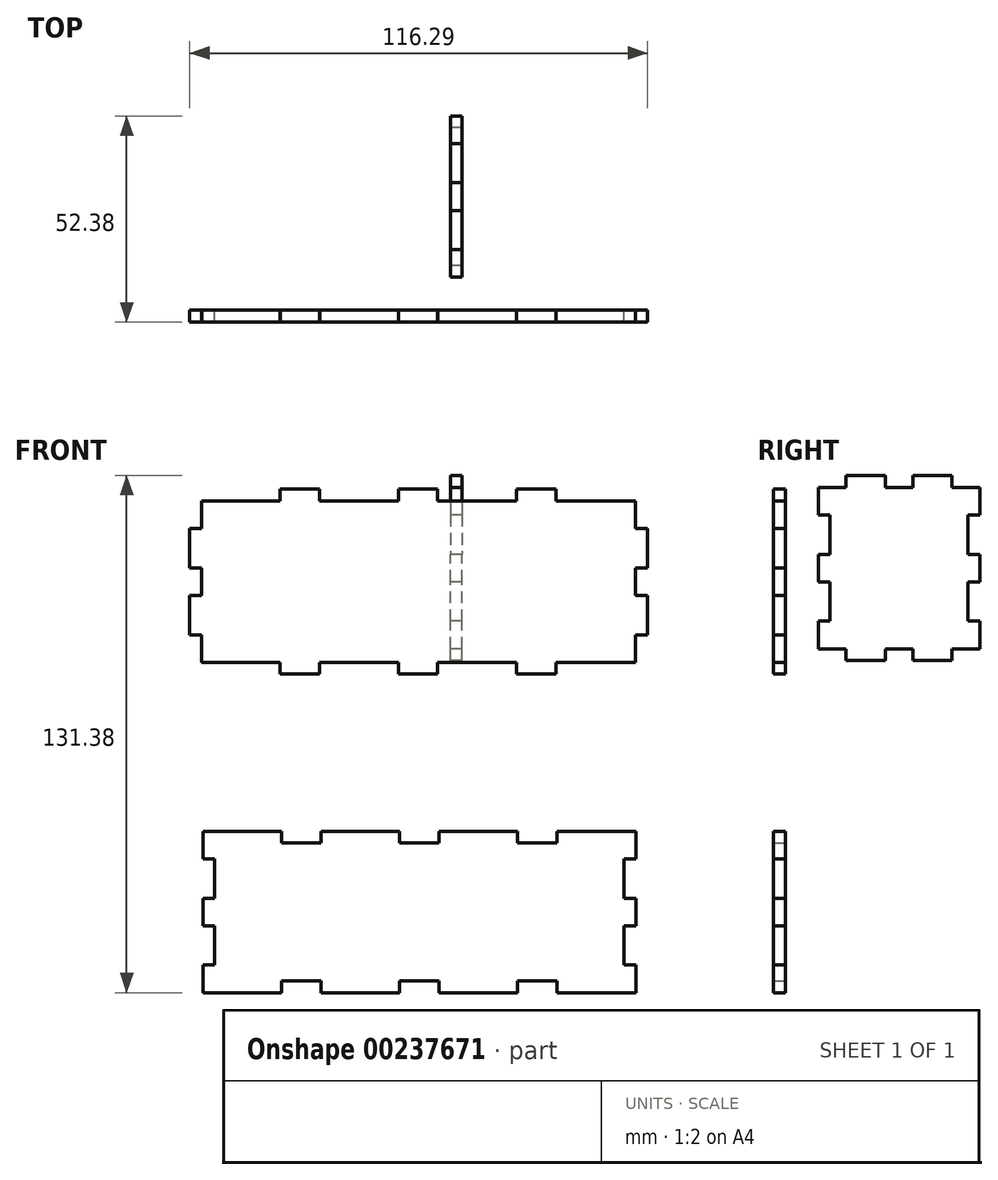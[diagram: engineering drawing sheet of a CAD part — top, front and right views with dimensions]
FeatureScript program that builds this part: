
annotation { "Feature Type Name" : "Feature", "Feature Type Description" : "" }
export const myFeature = defineFeature(function(context is Context, id is Id, definition is map)
    precondition{}
    {
        {
            var Q0;
            Q0=qCreatedBy(makeId("Front.planeOp"),FACE);
            var sketch = newSketch(context, id + "F0", { "sketchPlane" : qUnion([Q0])});
            skLineSegment(sketch, "E0", {"start": v(-62.87, -67.73) * mm, "end": v(-62.87, -60.73) * mm});
            skLineSegment(sketch, "E1", {"start": v(-62.87, -60.73) * mm, "end": v(-59.87, -60.73) * mm});
            skLineSegment(sketch, "E2", {"start": v(-59.87, -60.73) * mm, "end": v(-59.87, -50.73) * mm});
            skLineSegment(sketch, "E3", {"start": v(-59.87, -50.73) * mm, "end": v(-62.87, -50.73) * mm});
            skLineSegment(sketch, "E4", {"start": v(-62.87, -50.73) * mm, "end": v(-62.87, -43.73) * mm});
            skLineSegment(sketch, "E5", {"start": v(-62.87, -43.73) * mm, "end": v(-59.87, -43.73) * mm});
            skLineSegment(sketch, "E6", {"start": v(-59.87, -43.73) * mm, "end": v(-59.87, -33.73) * mm});
            skLineSegment(sketch, "E7", {"start": v(-59.87, -33.73) * mm, "end": v(-62.87, -33.73) * mm});
            skLineSegment(sketch, "E8", {"start": v(-62.87, -33.73) * mm, "end": v(-62.87, -26.73) * mm});
            skLineSegment(sketch, "E9", {"start": v(-62.87, -26.73) * mm, "end": v(-42.87, -26.73) * mm});
            skLineSegment(sketch, "E10", {"start": v(-42.87, -26.73) * mm, "end": v(-42.87, -29.73) * mm});
            skLineSegment(sketch, "E11", {"start": v(-42.87, -29.73) * mm, "end": v(-32.87, -29.73) * mm});
            skLineSegment(sketch, "E12", {"start": v(-32.87, -29.73) * mm, "end": v(-32.87, -26.73) * mm});
            skLineSegment(sketch, "E13", {"start": v(-32.87, -26.73) * mm, "end": v(-12.87, -26.73) * mm});
            skLineSegment(sketch, "E14", {"start": v(-12.87, -26.73) * mm, "end": v(-12.87, -29.73) * mm});
            skLineSegment(sketch, "E15", {"start": v(-12.87, -29.73) * mm, "end": v(-2.87, -29.73) * mm});
            skLineSegment(sketch, "E16", {"start": v(-2.87, -29.73) * mm, "end": v(-2.87, -26.73) * mm});
            skLineSegment(sketch, "E17", {"start": v(-2.87, -26.73) * mm, "end": v(17.13, -26.73) * mm});
            skLineSegment(sketch, "E18", {"start": v(17.13, -26.73) * mm, "end": v(17.13, -29.73) * mm});
            skLineSegment(sketch, "E19", {"start": v(17.13, -29.73) * mm, "end": v(27.13, -29.73) * mm});
            skLineSegment(sketch, "E20", {"start": v(27.13, -29.73) * mm, "end": v(27.13, -26.73) * mm});
            skLineSegment(sketch, "E21", {"start": v(27.13, -26.73) * mm, "end": v(47.13, -26.73) * mm});
            skLineSegment(sketch, "E22", {"start": v(47.13, -26.73) * mm, "end": v(47.13, -33.73) * mm});
            skLineSegment(sketch, "E23", {"start": v(47.13, -33.73) * mm, "end": v(44.13, -33.73) * mm});
            skLineSegment(sketch, "E24", {"start": v(44.13, -33.73) * mm, "end": v(44.13, -43.73) * mm});
            skLineSegment(sketch, "E25", {"start": v(44.13, -43.73) * mm, "end": v(47.13, -43.73) * mm});
            skLineSegment(sketch, "E26", {"start": v(47.13, -43.73) * mm, "end": v(47.13, -51.3) * mm});
            skLineSegment(sketch, "E27.MirrorCS", {"start": v(-59.87, -43.73) * mm, "end": v(-62.87, -43.73) * mm});
            skLineSegment(sketch, "E28.MirrorCS", {"start": v(-62.87, -50.73) * mm, "end": v(-59.87, -50.73) * mm});
            skLineSegment(sketch, "E29.MirrorCS", {"start": v(17.13, -67.73) * mm, "end": v(17.13, -64.73) * mm});
            skLineSegment(sketch, "E30.MirrorCS", {"start": v(-42.87, -67.73) * mm, "end": v(-42.87, -64.73) * mm});
            skLineSegment(sketch, "E31.MirrorCS", {"start": v(-59.87, -60.73) * mm, "end": v(-62.87, -60.73) * mm});
            skLineSegment(sketch, "E32.MirrorCS", {"start": v(44.13, -50.73) * mm, "end": v(47.13, -50.73) * mm});
            skLineSegment(sketch, "E33.MirrorCS", {"start": v(-12.87, -67.73) * mm, "end": v(-12.87, -64.73) * mm});
            skLineSegment(sketch, "E34.MirrorCS", {"start": v(47.13, -60.73) * mm, "end": v(44.13, -60.73) * mm});
            skLineSegment(sketch, "E35.MirrorCS", {"start": v(27.13, -64.73) * mm, "end": v(27.13, -67.73) * mm});
            skLineSegment(sketch, "E36.MirrorCS", {"start": v(-32.87, -64.73) * mm, "end": v(-32.87, -67.73) * mm});
            skLineSegment(sketch, "E37.MirrorCS", {"start": v(-2.87, -64.73) * mm, "end": v(-2.87, -67.73) * mm});
            skLineSegment(sketch, "E38.MirrorCS", {"start": v(-12.87, -64.73) * mm, "end": v(-2.87, -64.73) * mm});
            skLineSegment(sketch, "E39.MirrorCS", {"start": v(-42.87, -64.73) * mm, "end": v(-32.87, -64.73) * mm});
            skLineSegment(sketch, "E40.MirrorCS", {"start": v(17.13, -64.73) * mm, "end": v(27.13, -64.73) * mm});
            skLineSegment(sketch, "E41.MirrorCS", {"start": v(-62.87, -43.73) * mm, "end": v(-62.87, -50.73) * mm});
            skLineSegment(sketch, "E42.MirrorCS", {"start": v(44.13, -60.73) * mm, "end": v(44.13, -50.73) * mm});
            skLineSegment(sketch, "E43.MirrorCS", {"start": v(27.13, -67.73) * mm, "end": v(47.13, -67.73) * mm});
            skLineSegment(sketch, "E44.MirrorCS", {"start": v(-32.87, -67.73) * mm, "end": v(-12.87, -67.73) * mm});
            skLineSegment(sketch, "E45.MirrorCS", {"start": v(-2.87, -67.73) * mm, "end": v(17.13, -67.73) * mm});
            skLineSegment(sketch, "E46.MirrorCS", {"start": v(-62.87, -60.73) * mm, "end": v(-62.87, -67.73) * mm});
            skLineSegment(sketch, "E47.MirrorCS", {"start": v(-62.87, -67.73) * mm, "end": v(-42.87, -67.73) * mm});
            skLineSegment(sketch, "E48.MirrorCS", {"start": v(47.13, -50.73) * mm, "end": v(47.13, -43.16) * mm});
            skLineSegment(sketch, "E49.MirrorCS", {"start": v(47.13, -67.73) * mm, "end": v(47.13, -60.73) * mm});
            skLineSegment(sketch, "E50.MirrorCS", {"start": v(-59.87, -50.73) * mm, "end": v(-59.87, -60.73) * mm});
            skLineSegment(sketch, "E51", {"start": v(-63.18, 57.19) * mm, "end": v(-43.18, 57.19) * mm});
            skLineSegment(sketch, "E52", {"start": v(-43.18, 57.19) * mm, "end": v(-43.18, 60.19) * mm});
            skLineSegment(sketch, "E53", {"start": v(-43.18, 60.19) * mm, "end": v(-33.18, 60.19) * mm});
            skLineSegment(sketch, "E54", {"start": v(-33.18, 60.19) * mm, "end": v(-33.18, 57.19) * mm});
            skLineSegment(sketch, "E55", {"start": v(-33.18, 57.19) * mm, "end": v(-13.18, 57.19) * mm});
            skLineSegment(sketch, "E56", {"start": v(-13.18, 57.19) * mm, "end": v(-13.18, 60.19) * mm});
            skLineSegment(sketch, "E57", {"start": v(-13.18, 60.19) * mm, "end": v(-3.18, 60.19) * mm});
            skLineSegment(sketch, "E58", {"start": v(-3.18, 60.19) * mm, "end": v(-3.18, 57.19) * mm});
            skLineSegment(sketch, "E59", {"start": v(-3.18, 57.19) * mm, "end": v(16.82, 57.19) * mm});
            skLineSegment(sketch, "E60", {"start": v(16.82, 57.19) * mm, "end": v(16.82, 60.19) * mm});
            skLineSegment(sketch, "E61", {"start": v(16.82, 60.19) * mm, "end": v(26.82, 60.19) * mm});
            skLineSegment(sketch, "E62", {"start": v(26.82, 60.19) * mm, "end": v(26.82, 57.19) * mm});
            skLineSegment(sketch, "E63", {"start": v(26.82, 57.19) * mm, "end": v(47.1, 57.19) * mm});
            skLineSegment(sketch, "E64", {"start": v(47.1, 57.19) * mm, "end": v(47.1, 50.19) * mm});
            skLineSegment(sketch, "E65", {"start": v(47.1, 50.19) * mm, "end": v(50.1, 50.19) * mm});
            skLineSegment(sketch, "E66", {"start": v(50.1, 50.19) * mm, "end": v(50.1, 40.19) * mm});
            skLineSegment(sketch, "E67", {"start": v(50.1, 40.19) * mm, "end": v(47.1, 40.19) * mm});
            skLineSegment(sketch, "E68", {"start": v(47.1, 40.19) * mm, "end": v(47.1, 33.19) * mm});
            skLineSegment(sketch, "E69", {"start": v(47.1, 33.19) * mm, "end": v(50.1, 33.19) * mm});
            skLineSegment(sketch, "E70", {"start": v(-63.18, 57.19) * mm, "end": v(-63.18, 50.19) * mm});
            skLineSegment(sketch, "E71", {"start": v(-63.18, 50.19) * mm, "end": v(-66.18, 50.19) * mm});
            skLineSegment(sketch, "E72", {"start": v(-66.18, 50.19) * mm, "end": v(-66.18, 40.19) * mm});
            skLineSegment(sketch, "E73", {"start": v(-66.18, 40.19) * mm, "end": v(-63.18, 40.19) * mm});
            skLineSegment(sketch, "E74", {"start": v(-63.18, 40.19) * mm, "end": v(-63.18, 33.19) * mm});
            skPoint(sketch, "E75.endSnap0", {"position": v(47.1, 36.69) * mm});
            skLineSegment(sketch, "E76.MirrorCS", {"start": v(47.1, 23.19) * mm, "end": v(50.1, 23.19) * mm});
            skLineSegment(sketch, "E77.MirrorCS", {"start": v(-43.18, 13.19) * mm, "end": v(-33.18, 13.19) * mm});
            skLineSegment(sketch, "E78.MirrorCS", {"start": v(26.82, 13.19) * mm, "end": v(26.82, 16.19) * mm});
            skLineSegment(sketch, "E79.MirrorCS", {"start": v(-66.18, 23.19) * mm, "end": v(-66.18, 33.19) * mm});
            skLineSegment(sketch, "E80.MirrorCS", {"start": v(-13.18, 16.19) * mm, "end": v(-13.18, 13.19) * mm});
            skLineSegment(sketch, "E81.MirrorCS", {"start": v(47.1, 16.19) * mm, "end": v(47.1, 23.19) * mm});
            skLineSegment(sketch, "E82.MirrorCS", {"start": v(-43.18, 16.19) * mm, "end": v(-43.18, 13.19) * mm});
            skLineSegment(sketch, "E83.MirrorCS", {"start": v(16.82, 13.19) * mm, "end": v(26.82, 13.19) * mm});
            skLineSegment(sketch, "E84.MirrorCS", {"start": v(-63.18, 23.19) * mm, "end": v(-66.18, 23.19) * mm});
            skLineSegment(sketch, "E85.MirrorCS", {"start": v(-33.18, 16.19) * mm, "end": v(-13.18, 16.19) * mm});
            skLineSegment(sketch, "E86.MirrorCS", {"start": v(-3.18, 16.19) * mm, "end": v(16.82, 16.19) * mm});
            skLineSegment(sketch, "E87.MirrorCS", {"start": v(26.82, 16.19) * mm, "end": v(47.1, 16.19) * mm});
            skLineSegment(sketch, "E88.MirrorCS", {"start": v(-63.18, 16.19) * mm, "end": v(-43.18, 16.19) * mm});
            skLineSegment(sketch, "E89.MirrorCS", {"start": v(50.1, 33.19) * mm, "end": v(47.1, 33.19) * mm});
            skLineSegment(sketch, "E90.MirrorCS", {"start": v(16.82, 16.19) * mm, "end": v(16.82, 13.19) * mm});
            skLineSegment(sketch, "E91.MirrorCS", {"start": v(-63.18, 16.19) * mm, "end": v(-63.18, 23.19) * mm});
            skLineSegment(sketch, "E92.MirrorCS", {"start": v(-33.18, 13.19) * mm, "end": v(-33.18, 16.19) * mm});
            skLineSegment(sketch, "E93.MirrorCS", {"start": v(-3.18, 13.19) * mm, "end": v(-3.18, 16.19) * mm});
            skLineSegment(sketch, "E94.MirrorCS", {"start": v(50.1, 23.19) * mm, "end": v(50.1, 33.19) * mm});
            skLineSegment(sketch, "E95.MirrorCS", {"start": v(-66.18, 33.19) * mm, "end": v(-63.18, 33.19) * mm});
            skLineSegment(sketch, "E96.MirrorCS", {"start": v(-13.18, 13.19) * mm, "end": v(-3.18, 13.19) * mm});
            skLineSegment(sketch, "E97.MirrorCS", {"start": v(-62.87, 117.1) * mm, "end": v(-62.87, 124.1) * mm, "construction": true});
            skLineSegment(sketch, "E98.MirrorCS", {"start": v(47.13, 117.1) * mm, "end": v(47.13, 124.67) * mm, "construction": true});
            skLineSegment(sketch, "E99.MirrorCS", {"start": v(-59.87, 124.1) * mm, "end": v(-59.87, 134.1) * mm, "construction": true});
            skLineSegment(sketch, "E100.MirrorCS", {"start": v(-62.87, 134.1) * mm, "end": v(-62.87, 141.1) * mm, "construction": true});
            skLineSegment(sketch, "E101.MirrorCS", {"start": v(-62.87, 134.1) * mm, "end": v(-59.87, 134.1) * mm, "construction": true});
            skLineSegment(sketch, "E102.MirrorCS", {"start": v(-62.87, 124.1) * mm, "end": v(-59.87, 124.1) * mm, "construction": true});
            skLineSegment(sketch, "E103.MirrorCS", {"start": v(-59.87, 117.1) * mm, "end": v(-62.87, 117.1) * mm, "construction": true});
            skLineSegment(sketch, "E104.MirrorCS", {"start": v(-12.87, 141.1) * mm, "end": v(-12.87, 138.1) * mm, "construction": true});
            skLineSegment(sketch, "E105.MirrorCS", {"start": v(47.13, 141.1) * mm, "end": v(47.13, 134.1) * mm, "construction": true});
            skLineSegment(sketch, "E106.MirrorCS", {"start": v(17.13, 100.1) * mm, "end": v(17.13, 103.1) * mm, "construction": true});
            skLineSegment(sketch, "E107.MirrorCS", {"start": v(44.13, 117.1) * mm, "end": v(47.13, 117.1) * mm, "construction": true});
            skLineSegment(sketch, "E108.MirrorCS", {"start": v(17.13, 138.1) * mm, "end": v(27.13, 138.1) * mm, "construction": true});
            skLineSegment(sketch, "E109.MirrorCS", {"start": v(44.13, 124.1) * mm, "end": v(47.13, 124.1) * mm, "construction": true});
            skLineSegment(sketch, "E110.MirrorCS", {"start": v(47.13, 124.1) * mm, "end": v(47.13, 116.53) * mm, "construction": true});
            skLineSegment(sketch, "E111.MirrorCS", {"start": v(-2.87, 100.1) * mm, "end": v(17.13, 100.1) * mm, "construction": true});
            skLineSegment(sketch, "E112.MirrorCS", {"start": v(44.13, 107.1) * mm, "end": v(44.13, 117.1) * mm, "construction": true});
            skLineSegment(sketch, "E113.MirrorCS", {"start": v(-42.87, 138.1) * mm, "end": v(-32.87, 138.1) * mm, "construction": true});
            skLineSegment(sketch, "E114.MirrorCS", {"start": v(27.13, 100.1) * mm, "end": v(47.13, 100.1) * mm, "construction": true});
            skLineSegment(sketch, "E115.MirrorCS", {"start": v(17.13, 103.1) * mm, "end": v(27.13, 103.1) * mm, "construction": true});
            skLineSegment(sketch, "E116.MirrorCS", {"start": v(-2.87, 141.1) * mm, "end": v(17.13, 141.1) * mm, "construction": true});
            skLineSegment(sketch, "E117.MirrorCS", {"start": v(-32.87, 138.1) * mm, "end": v(-32.87, 141.1) * mm, "construction": true});
            skLineSegment(sketch, "E118.MirrorCS", {"start": v(17.13, 141.1) * mm, "end": v(17.13, 138.1) * mm, "construction": true});
            skLineSegment(sketch, "E119.MirrorCS", {"start": v(47.13, 134.1) * mm, "end": v(44.13, 134.1) * mm, "construction": true});
            skLineSegment(sketch, "E120.MirrorCS", {"start": v(47.13, 100.1) * mm, "end": v(47.13, 107.1) * mm, "construction": true});
            skLineSegment(sketch, "E121.MirrorCS", {"start": v(-2.87, 138.1) * mm, "end": v(-2.87, 141.1) * mm, "construction": true});
            skLineSegment(sketch, "E122.MirrorCS", {"start": v(-42.87, 141.1) * mm, "end": v(-42.87, 138.1) * mm, "construction": true});
            skLineSegment(sketch, "E123.MirrorCS", {"start": v(-32.87, 100.1) * mm, "end": v(-12.87, 100.1) * mm, "construction": true});
            skLineSegment(sketch, "E124.MirrorCS", {"start": v(-12.87, 100.1) * mm, "end": v(-12.87, 103.1) * mm, "construction": true});
            skLineSegment(sketch, "E125.MirrorCS", {"start": v(-12.87, 103.1) * mm, "end": v(-2.87, 103.1) * mm, "construction": true});
            skLineSegment(sketch, "E126.MirrorCS", {"start": v(44.13, 134.1) * mm, "end": v(44.13, 124.1) * mm, "construction": true});
            skLineSegment(sketch, "E127.MirrorCS", {"start": v(-62.87, 120.6) * mm, "end": v(59.39, 120.6) * mm, "construction": true});
            skLineSegment(sketch, "E128.MirrorCS", {"start": v(-62.87, 141.1) * mm, "end": v(-62.87, 134.1) * mm, "construction": true});
            skLineSegment(sketch, "E129.MirrorCS", {"start": v(-59.87, 134.1) * mm, "end": v(-59.87, 124.1) * mm, "construction": true});
            skLineSegment(sketch, "E130.MirrorCS", {"start": v(-59.87, 124.1) * mm, "end": v(-62.87, 124.1) * mm, "construction": true});
            skLineSegment(sketch, "E131.MirrorCS", {"start": v(-62.87, 117.1) * mm, "end": v(-59.87, 117.1) * mm, "construction": true});
            skLineSegment(sketch, "E132.MirrorCS", {"start": v(-62.87, 124.1) * mm, "end": v(-62.87, 117.1) * mm, "construction": true});
            skLineSegment(sketch, "E133.MirrorCS", {"start": v(27.13, 103.1) * mm, "end": v(27.13, 100.1) * mm, "construction": true});
            skLineSegment(sketch, "E134.MirrorCS", {"start": v(-59.87, 117.1) * mm, "end": v(-59.87, 107.1) * mm, "construction": true});
            skLineSegment(sketch, "E135.MirrorCS", {"start": v(-32.87, 141.1) * mm, "end": v(-12.87, 141.1) * mm, "construction": true});
            skLineSegment(sketch, "E136.MirrorCS", {"start": v(27.13, 138.1) * mm, "end": v(27.13, 141.1) * mm, "construction": true});
            skLineSegment(sketch, "E137.MirrorCS", {"start": v(-59.87, 107.1) * mm, "end": v(-62.87, 107.1) * mm, "construction": true});
            skLineSegment(sketch, "E138.MirrorCS", {"start": v(-62.87, 107.1) * mm, "end": v(-62.87, 100.1) * mm, "construction": true});
            skLineSegment(sketch, "E139.MirrorCS", {"start": v(-62.87, 100.1) * mm, "end": v(-42.87, 100.1) * mm, "construction": true});
            skLineSegment(sketch, "E140.MirrorCS", {"start": v(-42.87, 100.1) * mm, "end": v(-42.87, 103.1) * mm, "construction": true});
            skLineSegment(sketch, "E141.MirrorCS", {"start": v(-42.87, 103.1) * mm, "end": v(-32.87, 103.1) * mm, "construction": true});
            skLineSegment(sketch, "E142.MirrorCS", {"start": v(-32.87, 103.1) * mm, "end": v(-32.87, 100.1) * mm, "construction": true});
            skLineSegment(sketch, "E143.MirrorCS", {"start": v(-12.87, 138.1) * mm, "end": v(-2.87, 138.1) * mm, "construction": true});
            skLineSegment(sketch, "E144.MirrorCS", {"start": v(47.13, 107.1) * mm, "end": v(44.13, 107.1) * mm, "construction": true});
            skLineSegment(sketch, "E145.MirrorCS", {"start": v(27.13, 141.1) * mm, "end": v(47.13, 141.1) * mm, "construction": true});
            skLineSegment(sketch, "E146.MirrorCS", {"start": v(-2.87, 103.1) * mm, "end": v(-2.87, 100.1) * mm, "construction": true});
            skLineSegment(sketch, "E147.MirrorCS", {"start": v(-62.87, 141.1) * mm, "end": v(-42.87, 141.1) * mm, "construction": true});
            skLineSegment(sketch, "E148.MirrorCS", {"start": v(-59.87, 134.1) * mm, "end": v(-62.87, 134.1) * mm, "construction": true});
            skSolve(sketch);
        }
        {
            var Q0;
            Q0 = qSketchRegion(id + "F0", true);
            extrude(context, id + "F1", {"entities" : qUnion([Q0]), "depth" : 3 * mm});
        }
        {
            var Q0;
            Q0=qCreatedBy(makeId("Right.planeOp"),FACE);
            var sketch = newSketch(context, id + "F2", { "sketchPlane" : qUnion([Q0])});
            skLineSegment(sketch, "E149", {"start": v(49.38, 19.65) * mm, "end": v(42.38, 19.65) * mm});
            skLineSegment(sketch, "E150", {"start": v(42.38, 19.65) * mm, "end": v(42.38, 16.65) * mm});
            skLineSegment(sketch, "E151", {"start": v(42.38, 16.65) * mm, "end": v(32.38, 16.65) * mm});
            skLineSegment(sketch, "E152", {"start": v(32.38, 16.65) * mm, "end": v(32.38, 19.65) * mm});
            skLineSegment(sketch, "E153", {"start": v(32.38, 19.65) * mm, "end": v(25.38, 19.65) * mm});
            skLineSegment(sketch, "E154", {"start": v(25.38, 19.65) * mm, "end": v(25.38, 16.65) * mm});
            skLineSegment(sketch, "E155", {"start": v(25.38, 16.65) * mm, "end": v(15.38, 16.65) * mm});
            skLineSegment(sketch, "E156", {"start": v(15.38, 16.65) * mm, "end": v(15.38, 19.65) * mm});
            skLineSegment(sketch, "E157", {"start": v(15.38, 19.65) * mm, "end": v(8.38, 19.65) * mm});
            skLineSegment(sketch, "E158", {"start": v(8.38, 19.65) * mm, "end": v(8.38, 26.65) * mm});
            skLineSegment(sketch, "E159", {"start": v(8.38, 26.65) * mm, "end": v(11.38, 26.65) * mm});
            skLineSegment(sketch, "E160", {"start": v(11.38, 26.65) * mm, "end": v(11.38, 36.65) * mm});
            skLineSegment(sketch, "E161", {"start": v(11.38, 36.65) * mm, "end": v(8.38, 36.65) * mm});
            skLineSegment(sketch, "E162", {"start": v(8.38, 36.65) * mm, "end": v(8.38, 43.65) * mm});
            skLineSegment(sketch, "E163", {"start": v(8.38, 43.65) * mm, "end": v(11.38, 43.65) * mm});
            skLineSegment(sketch, "E164", {"start": v(49.38, 19.65) * mm, "end": v(49.38, 26.65) * mm});
            skLineSegment(sketch, "E165", {"start": v(49.38, 26.65) * mm, "end": v(46.38, 26.65) * mm});
            skLineSegment(sketch, "E166", {"start": v(46.38, 26.65) * mm, "end": v(46.38, 36.65) * mm});
            skLineSegment(sketch, "E167", {"start": v(46.38, 36.65) * mm, "end": v(49.38, 36.65) * mm});
            skLineSegment(sketch, "E168", {"start": v(49.38, 36.65) * mm, "end": v(49.38, 43.65) * mm});
            skLineSegment(sketch, "E169.MirrorCS", {"start": v(25.38, 60.65) * mm, "end": v(25.38, 63.65) * mm});
            skLineSegment(sketch, "E170.MirrorCS", {"start": v(15.38, 63.65) * mm, "end": v(15.38, 60.65) * mm});
            skLineSegment(sketch, "E171.MirrorCS", {"start": v(32.38, 63.65) * mm, "end": v(32.38, 60.65) * mm});
            skLineSegment(sketch, "E172.MirrorCS", {"start": v(42.38, 60.65) * mm, "end": v(42.38, 63.65) * mm});
            skLineSegment(sketch, "E173.MirrorCS", {"start": v(25.38, 63.65) * mm, "end": v(15.38, 63.65) * mm});
            skLineSegment(sketch, "E174.MirrorCS", {"start": v(32.38, 60.65) * mm, "end": v(25.38, 60.65) * mm});
            skLineSegment(sketch, "E175.MirrorCS", {"start": v(15.38, 60.65) * mm, "end": v(8.38, 60.65) * mm});
            skLineSegment(sketch, "E176.MirrorCS", {"start": v(8.38, 60.65) * mm, "end": v(8.38, 53.65) * mm});
            skLineSegment(sketch, "E177.MirrorCS", {"start": v(8.38, 53.65) * mm, "end": v(11.38, 53.65) * mm});
            skLineSegment(sketch, "E178.MirrorCS", {"start": v(11.38, 53.65) * mm, "end": v(11.38, 43.65) * mm});
            skLineSegment(sketch, "E179.MirrorCS", {"start": v(11.38, 43.65) * mm, "end": v(8.38, 43.65) * mm});
            skLineSegment(sketch, "E180.MirrorCS", {"start": v(42.38, 63.65) * mm, "end": v(32.38, 63.65) * mm});
            skLineSegment(sketch, "E181.MirrorCS", {"start": v(49.38, 43.65) * mm, "end": v(49.38, 36.65) * mm});
            skLineSegment(sketch, "E182.MirrorCS", {"start": v(46.38, 43.65) * mm, "end": v(49.38, 43.65) * mm});
            skLineSegment(sketch, "E183.MirrorCS", {"start": v(49.38, 53.65) * mm, "end": v(46.38, 53.65) * mm});
            skLineSegment(sketch, "E184.MirrorCS", {"start": v(49.38, 60.65) * mm, "end": v(42.38, 60.65) * mm});
            skLineSegment(sketch, "E185.MirrorCS", {"start": v(49.38, 60.65) * mm, "end": v(49.38, 53.65) * mm});
            skLineSegment(sketch, "E186.MirrorCS", {"start": v(46.38, 53.65) * mm, "end": v(46.38, 43.65) * mm});
            skLineSegment(sketch, "E187.MirrorCS", {"start": v(8.38, 43.65) * mm, "end": v(8.38, 36.65) * mm});
            skLineSegment(sketch, "E188.MirrorCS", {"start": v(8.38, 36.65) * mm, "end": v(11.38, 36.65) * mm});
            skPoint(sketch, "E189.endSnap0", {"position": v(28.88, 19.65) * mm});
            skSolve(sketch);
        }
        {
            var Q0;
            Q0=makeQuery(id+"F2.imprint","IMPRINT",FACE,{"disambiguationData":[TD([[makeQuery(id+"F2.imprint","IMPRINT",EDGE,{"derivedFrom":sQuery(id+"F2.wireOp",EDGE,"E149")}),-1.0]])]});
            extrude(context, id + "F3", {"entities" : qUnion([Q0]), "depth" : 3 * mm});
        }
    });
